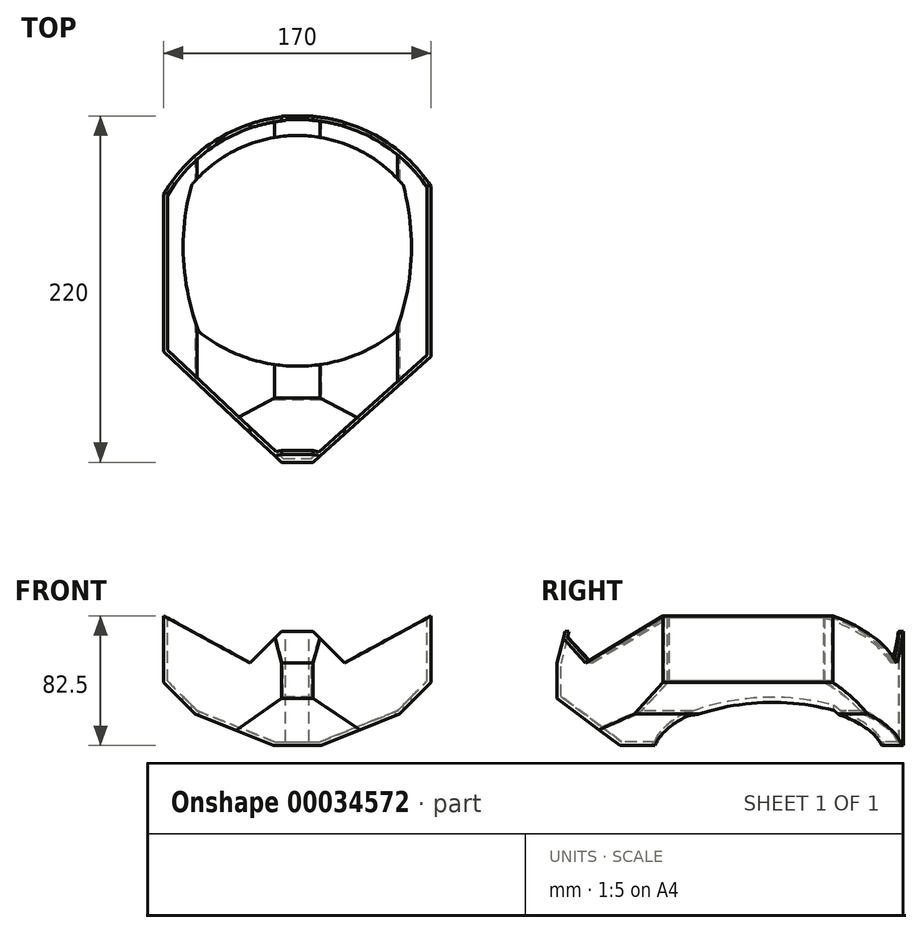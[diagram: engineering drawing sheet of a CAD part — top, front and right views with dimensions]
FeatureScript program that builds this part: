
annotation { "Feature Type Name" : "Feature", "Feature Type Description" : "" }
export const myFeature = defineFeature(function(context is Context, id is Id, definition is map)
    precondition{}
    {
        {
            var Q0;
            Q0=qCreatedBy(makeId("Front.planeOp"),FACE);
            var sketch = newSketch(context, id + "F0", { "sketchPlane" : qUnion([Q0])});
            skLineSegment(sketch, "E0", {"start": v(-30, 0) * mm, "end": v(-10, 20) * mm});
            skLineSegment(sketch, "E1", {"start": v(-10, 20) * mm, "end": v(10, 20) * mm});
            skLineSegment(sketch, "E2", {"start": v(10, 20) * mm, "end": v(30, 0) * mm});
            skLineSegment(sketch, "E3", {"start": v(30, 0) * mm, "end": v(85, 30) * mm});
            skLineSegment(sketch, "E4", {"start": v(-30, 0) * mm, "end": v(-85, 30) * mm});
            skLineSegment(sketch, "E5", {"start": v(-85, 30) * mm, "end": v(-85, -12.5) * mm});
            skLineSegment(sketch, "E6", {"start": v(-15, -52.5) * mm, "end": v(15, -52.5) * mm});
            skLineSegment(sketch, "E7", {"start": v(85, -12.5) * mm, "end": v(85, 30) * mm});
            skLineSegment(sketch, "E8", {"start": v(-85, -12.5) * mm, "end": v(-65, -32.5) * mm});
            skLineSegment(sketch, "E9", {"start": v(65, -32.5) * mm, "end": v(85, -12.5) * mm});
            skPoint(sketch, "E10.orphan", {"position": v(-85, -52.5) * mm});
            skPoint(sketch, "E11.orphan", {"position": v(85, -52.5) * mm});
            skLineSegment(sketch, "E12", {"start": v(-65, -32.5) * mm, "end": v(-15, -52.5) * mm});
            skLineSegment(sketch, "E13", {"start": v(15, -52.5) * mm, "end": v(65, -32.5) * mm});
            skSolve(sketch);
        }
        {
            var Q0;
            Q0 = qSketchRegion(id + "F0", true);
            extrude(context, id + "F1", {"entities" : qUnion([Q0]), "oppositeDirection" : true, "depth" : 220 * mm});
        }
        {
            var Q0;
            Q0=makeQuery(id+"F1.opExtrude","SWEPT_FACE",FACE,{"disambiguationData":[OSD([sQuery(id+"F0.wireOp",EDGE,"E7")])]});
            var sketch = newSketch(context, id + "F2", { "sketchPlane" : qUnion([Q0])});
            skLineSegment(sketch, "E14", {"start": v(5, 20) * mm, "end": v(0, 0) * mm});
            skLineSegment(sketch, "E15", {"start": v(0, 0) * mm, "end": v(0, -22.5) * mm});
            skLineSegment(sketch, "E16", {"start": v(0, -22.5) * mm, "end": v(40, -52.5) * mm});
            skLineSegment(sketch, "E17", {"start": v(5, 20) * mm, "end": v(0, 20) * mm});
            skLineSegment(sketch, "E18", {"start": v(0, 20) * mm, "end": v(0, 0) * mm});
            skLineSegment(sketch, "E19", {"start": v(40, -52.5) * mm, "end": v(0, -52.5) * mm});
            skLineSegment(sketch, "E20", {"start": v(0, -52.5) * mm, "end": v(0, -22.5) * mm});
            skSolve(sketch);
        }
        {
            var Q0;
            Q0 = qSketchRegion(id + "F2", true);
            var Q1;
            Q1=makeQuery(id+"F1.opExtrude","SWEPT_FACE",FACE,{"disambiguationData":[OSD([sQuery(id+"F0.wireOp",EDGE,"E5")])]});
            extrude(context, id + "F3", {"entities" : qUnion([Q0]), "operationType" : NewBodyOperationType.REMOVE, "endBound" : BoundingType.UP_TO_SURFACE, "oppositeDirection" : true, "endBoundEntityFace" : qUnion([Q1]), "depth" : 25 * mm});
        }
        {
            var Q0;
            Q0=makeQuery(id+"F1.opExtrude","SWEPT_FACE",FACE,{"disambiguationData":[OSD([sQuery(id+"F0.wireOp",EDGE,"E1")])]});
            var sketch = newSketch(context, id + "F4", { "sketchPlane" : qUnion([Q0])});
            skLineSegment(sketch, "E21", {"start": v(88.2, 70) * mm, "end": v(88.2, 170) * mm});
            skLineSegment(sketch, "E22", {"start": v(-85, 170) * mm, "end": v(-85, 70.2) * mm});
            skLineSegment(sketch, "E23", {"start": v(83.2, 163.56) * mm, "end": v(83.2, 70.52) * mm});
            skLineSegment(sketch, "E24", {"start": v(-80, 163.56) * mm, "end": v(-80, 70.52) * mm});
            skArc(sketch, "E25", {"start": v(88.2, 170) * mm, "mid": v(1.6, 220) * mm, "end": v(-85, 170) * mm});
            skArc(sketch, "E26.0", {"start": v(83.2, 163.56) * mm, "mid": v(1.6, 212.5) * mm, "end": v(-80, 163.56) * mm});
            skLineSegment(sketch, "E27", {"start": v(88.2, 170) * mm, "end": v(88.2, 220) * mm});
            skLineSegment(sketch, "E28", {"start": v(88.2, 220) * mm, "end": v(-85, 220) * mm});
            skLineSegment(sketch, "E29", {"start": v(-85, 220) * mm, "end": v(-85, 170) * mm});
            skLineSegment(sketch, "E30", {"start": v(83.2, 163.56) * mm, "end": v(88.2, 170) * mm, "construction": true});
            skLineSegment(sketch, "E31", {"start": v(-85, 170) * mm, "end": v(88.2, 170) * mm, "construction": true});
            skLineSegment(sketch, "E32", {"start": v(-80, 70.52) * mm, "end": v(83.2, 70.52) * mm, "construction": true});
            skLineSegment(sketch, "E33", {"start": v(-80, 163.56) * mm, "end": v(83.2, 163.56) * mm, "construction": true});
            skLineSegment(sketch, "E34", {"start": v(-80, 70.52) * mm, "end": v(-10, 5) * mm});
            skLineSegment(sketch, "E35", {"start": v(-10, 5) * mm, "end": v(10, 5) * mm});
            skLineSegment(sketch, "E36", {"start": v(10, 5) * mm, "end": v(83.2, 70.52) * mm});
            skLineSegment(sketch, "E37", {"start": v(88.2, 70) * mm, "end": v(10, 0) * mm});
            skLineSegment(sketch, "E38", {"start": v(-10, 0) * mm, "end": v(-85, 70.2) * mm});
            skLineSegment(sketch, "E39", {"start": v(-10, 0) * mm, "end": v(10, 0) * mm});
            skLineSegment(sketch, "E40", {"start": v(-10, 5) * mm, "end": v(-10, 0) * mm, "construction": true});
            skLineSegment(sketch, "E41", {"start": v(10, 5) * mm, "end": v(10, 0) * mm, "construction": true});
            skLineSegment(sketch, "E42", {"start": v(88.2, 70) * mm, "end": v(88.2, 0) * mm});
            skLineSegment(sketch, "E43", {"start": v(88.2, 0) * mm, "end": v(-85, 0) * mm});
            skLineSegment(sketch, "E44", {"start": v(-85, 0) * mm, "end": v(-85, 70.2) * mm});
            skSolve(sketch);
        }
        {
            var Q0;
            {var subQ2=sQuery(id+"F4.wireOp",EDGE,"E38");Q0=makeQuery(id+"F4.imprint","IMPRINT",FACE,{"disambiguationData":[TD([[makeQuery(id+"F4.imprint","IMPRINT",EDGE,{"derivedFrom":subQ2}),1.0]])]});}
            var Q1;
            {var subQ2=sQuery(id+"F4.wireOp",EDGE,"E37");Q1=makeQuery(id+"F4.imprint","IMPRINT",FACE,{"disambiguationData":[TD([[makeQuery(id+"F4.imprint","IMPRINT",EDGE,{"derivedFrom":subQ2}),1.0]])]});}
            var Q2;
            {var subQ5=sQuery(id+"F4.wireOp",EDGE,"E29");Q2=makeQuery(id+"F4.imprint","IMPRINT",FACE,{"disambiguationData":[TD([[makeQuery(id+"F4.imprint","IMPRINT",EDGE,{"derivedFrom":subQ5}),1.0]])]});}
            var Q3;
            {var subQ5=sQuery(id+"F4.wireOp",EDGE,"E27");Q3=makeQuery(id+"F4.imprint","IMPRINT",FACE,{"disambiguationData":[TD([[makeQuery(id+"F4.imprint","IMPRINT",EDGE,{"derivedFrom":subQ5}),1.0]])]});}
            var Q4;
            Q4=makeQuery(id+"F1.opExtrude","SWEPT_FACE",FACE,{"disambiguationData":[OSD([sQuery(id+"F0.wireOp",EDGE,"E6")])]});
            extrude(context, id + "F5", {"entities" : qUnion([Q0, Q1, Q2, Q3]), "operationType" : NewBodyOperationType.REMOVE, "endBound" : BoundingType.SYMMETRIC, "oppositeDirection" : true, "endBoundEntityFace" : qUnion([Q4]), "depth" : 200 * mm});
        }
        {
            var Q0;
            Q0=makeQuery(id+"F1.opExtrude","SWEPT_FACE",FACE,{"disambiguationData":[OSD([sQuery(id+"F0.wireOp",EDGE,"E3")])]});
            var Q1;
            Q1=makeQuery(id+"F1.opExtrude","SWEPT_FACE",FACE,{"disambiguationData":[OSD([sQuery(id+"F0.wireOp",EDGE,"E2")])]});
            var Q2;
            Q2=makeQuery(id+"F1.opExtrude","SWEPT_FACE",FACE,{"disambiguationData":[OSD([sQuery(id+"F0.wireOp",EDGE,"E1")])]});
            var Q3;
            Q3=makeQuery(id+"F1.opExtrude","SWEPT_FACE",FACE,{"disambiguationData":[OSD([sQuery(id+"F0.wireOp",EDGE,"E4")])]});
            var Q4;
            Q4=makeQuery(id+"F1.opExtrude","SWEPT_FACE",FACE,{"disambiguationData":[OSD([sQuery(id+"F0.wireOp",EDGE,"E0")])]});
            shell(context, id + "F6", {"entities" : qUnion([Q0, Q1, Q2, Q3, Q4]), "thickness" : 2.5 * mm});
        }
        {
            var Q0;
            Q0=qCreatedBy(makeId("Top.planeOp"),FACE);
            var sketch = newSketch(context, id + "F7", { "sketchPlane" : qUnion([Q0])});
            skArc(sketch, "E45", {"start": v(67.31, 175.9) * mm, "mid": v(0, 207.5) * mm, "end": v(-67.31, 175.9) * mm});
            skArc(sketch, "E46", {"start": v(-62.5, 82.95) * mm, "mid": v(0, 61.01) * mm, "end": v(62.5, 82.95) * mm});
            skLineSegment(sketch, "E47", {"start": v(-62.5, 82.95) * mm, "end": v(62.5, 82.95) * mm, "construction": true});
            skArc(sketch, "E48", {"start": v(-67.31, 175.9) * mm, "mid": v(-72.3, 129.04) * mm, "end": v(-62.5, 82.95) * mm});
            skArc(sketch, "E49", {"start": v(62.5, 82.95) * mm, "mid": v(72.3, 129.04) * mm, "end": v(67.31, 175.9) * mm});
            skLineSegment(sketch, "E50", {"start": v(0, 61.01) * mm, "end": v(0, 0) * mm, "construction": true});
            skSolve(sketch);
        }
        {
            var Q0;
            Q0 = qSketchRegion(id + "F7", true);
            extrude(context, id + "F8", {"entities" : qUnion([Q0]), "operationType" : NewBodyOperationType.REMOVE, "endBound" : BoundingType.THROUGH_ALL, "oppositeDirection" : true, "depth" : 25 * mm});
        }
    });
